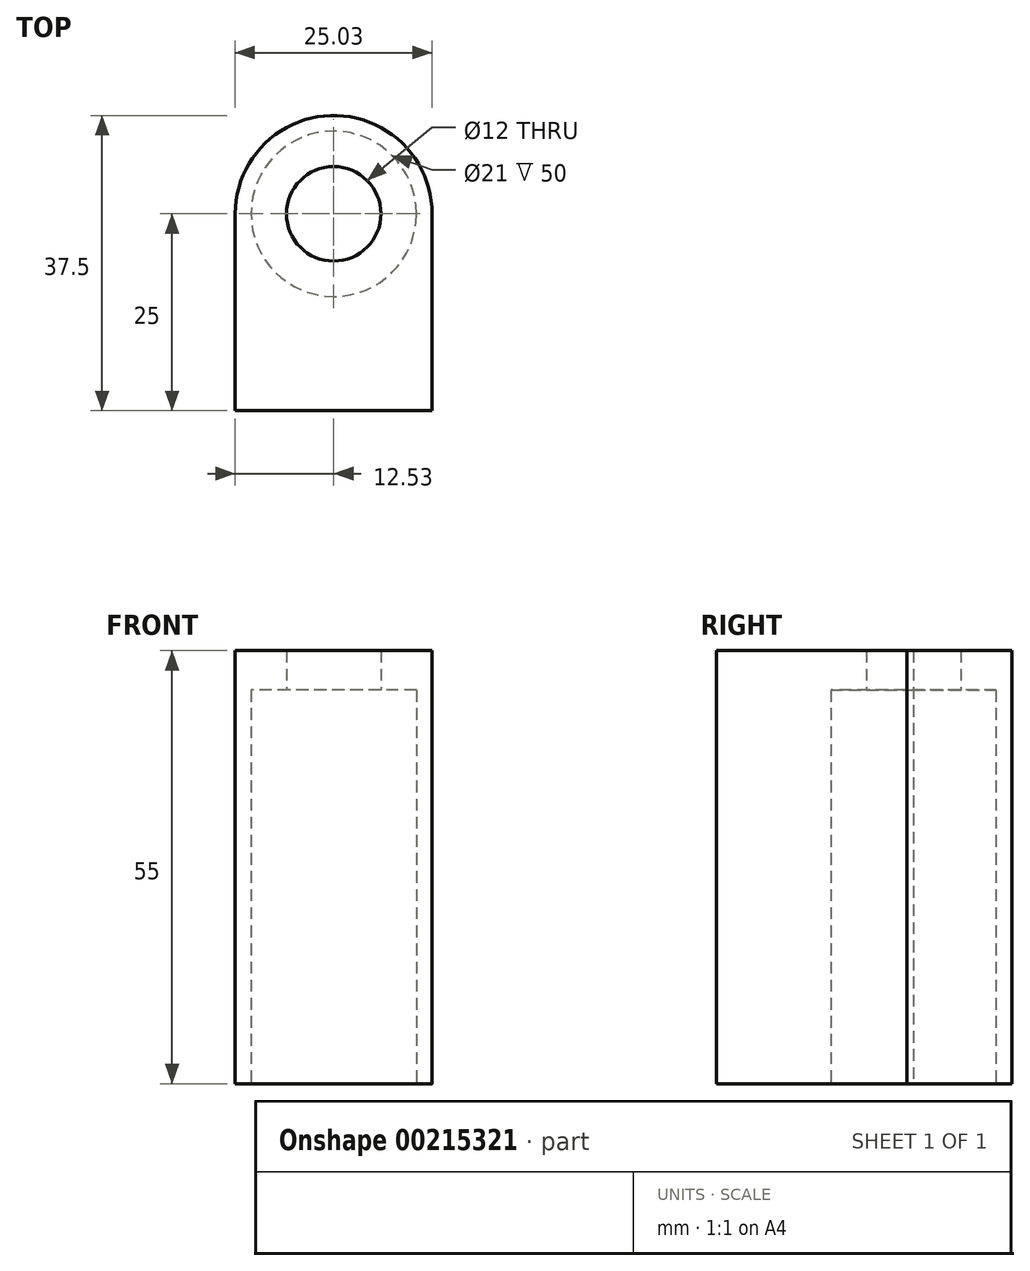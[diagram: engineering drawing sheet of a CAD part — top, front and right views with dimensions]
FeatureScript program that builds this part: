
annotation { "Feature Type Name" : "Feature", "Feature Type Description" : "" }
export const myFeature = defineFeature(function(context is Context, id is Id, definition is map)
    precondition{}
    {
        {
            var Q0;
            Q0=qCreatedBy(makeId("Top.planeOp"),FACE);
            var sketch = newSketch(context, id + "F4", { "sketchPlane" : qUnion([Q0])});
            skCircle(sketch, "E0", {"center": v(0, 0) * mm, "radius": 12.5 * mm});
            skSolve(sketch);
        }
        {
            var Q0;
            Q0=makeQuery(id+"F4.imprint","IMPRINT",FACE,{"disambiguationData":[TD([[makeQuery(id+"F4.imprint","IMPRINT",EDGE,{"derivedFrom":sQuery(id+"F4.wireOp",EDGE,"E0")}),1.0]])]});
            extrude(context, id + "F0", {"entities" : qUnion([Q0]), "depth" : 55 * mm});
        }
        {
            var Q0;
            Q0=qCreatedBy(makeId("Top.planeOp"),FACE);
            var sketch = newSketch(context, id + "F1", { "sketchPlane" : qUnion([Q0])});
            skLineSegment(sketch, "E1.bottom", {"start": v(-12.53, 0) * mm, "end": v(12.47, 0) * mm});
            skLineSegment(sketch, "E1.top", {"start": v(-12.53, -25) * mm, "end": v(12.47, -25) * mm});
            skLineSegment(sketch, "E1.left", {"start": v(-12.53, 0) * mm, "end": v(-12.53, -25) * mm});
            skLineSegment(sketch, "E1.right", {"start": v(12.47, 0) * mm, "end": v(12.47, -25) * mm});
            skSolve(sketch);
        }
        {
            var Q0;
            Q0=makeQuery(id+"F1.imprint","IMPRINT",FACE,{"disambiguationData":[TD([[makeQuery(id+"F1.imprint","IMPRINT",EDGE,{"derivedFrom":sQuery(id+"F1.wireOp",EDGE,"E1.bottom")}),-1.0]])]});
            extrude(context, id + "F5", {"entities" : qUnion([Q0]), "operationType" : NewBodyOperationType.ADD, "depth" : 55 * mm});
        }
        {
            var Q0;
            Q0=makeQuery(id+"F5.boolean.opBoolean","MERGE",FACE,{"derivedFrom":[makeQuery(id+"F0.opExtrude","CAP_FACE",FACE,{"disambiguationData":[OSD([sQuery(id+"F4.wireOp",EDGE,"E0")])],"isStart":true}),makeQuery(id+"F5.opExtrude","CAP_FACE",FACE,{"disambiguationData":[OSD([sQuery(id+"F1.wireOp",EDGE,"E1.bottom"),sQuery(id+"F1.wireOp",EDGE,"E1.top"),sQuery(id+"F1.wireOp",EDGE,"E1.left"),sQuery(id+"F1.wireOp",EDGE,"E1.right")])],"isStart":true})]});
            var sketch = newSketch(context, id + "F6", { "sketchPlane" : qUnion([Q0])});
            skPoint(sketch, "E2", {"position": v(0, 0) * mm});
            skSolve(sketch);
        }
        {
            var Q0;
            Q0=sQuery(id+"F6.wireOp",VERTEX,"E2");
            var Q1;
            Q1=makeQuery(id+"F0.opExtrude","SWEPT_BODY",BODY,{"disambiguationData":[OSD([sQuery(id+"F4.wireOp",EDGE,"E0")])]});
            hole(context, id + "F2", {"style" : HoleStyle.SIMPLE, "endStyle" : HoleEndStyle.THROUGH, "holeDiameter" : 12 * mm, "locations" : qUnion([Q0]), "scope" : qUnion([Q1]), "isTappedThrough" : true});
        }
        {
            var Q0;
            Q0=qCreatedBy(makeId("Top.planeOp"),FACE);
            var sketch = newSketch(context, id + "F7", { "sketchPlane" : qUnion([Q0])});
            skCircle(sketch, "E3", {"center": v(0, 0) * mm, "radius": 10.5 * mm});
            skSolve(sketch);
        }
        {
            var Q0;
            Q0=makeQuery(id+"F7.imprint","IMPRINT",FACE,{"disambiguationData":[TD([[makeQuery(id+"F7.imprint","IMPRINT",EDGE,{"derivedFrom":sQuery(id+"F7.wireOp",EDGE,"E3")}),1.0]])]});
            extrude(context, id + "F3", {"entities" : qUnion([Q0]), "operationType" : NewBodyOperationType.REMOVE, "depth" : 50 * mm});
        }
    });
